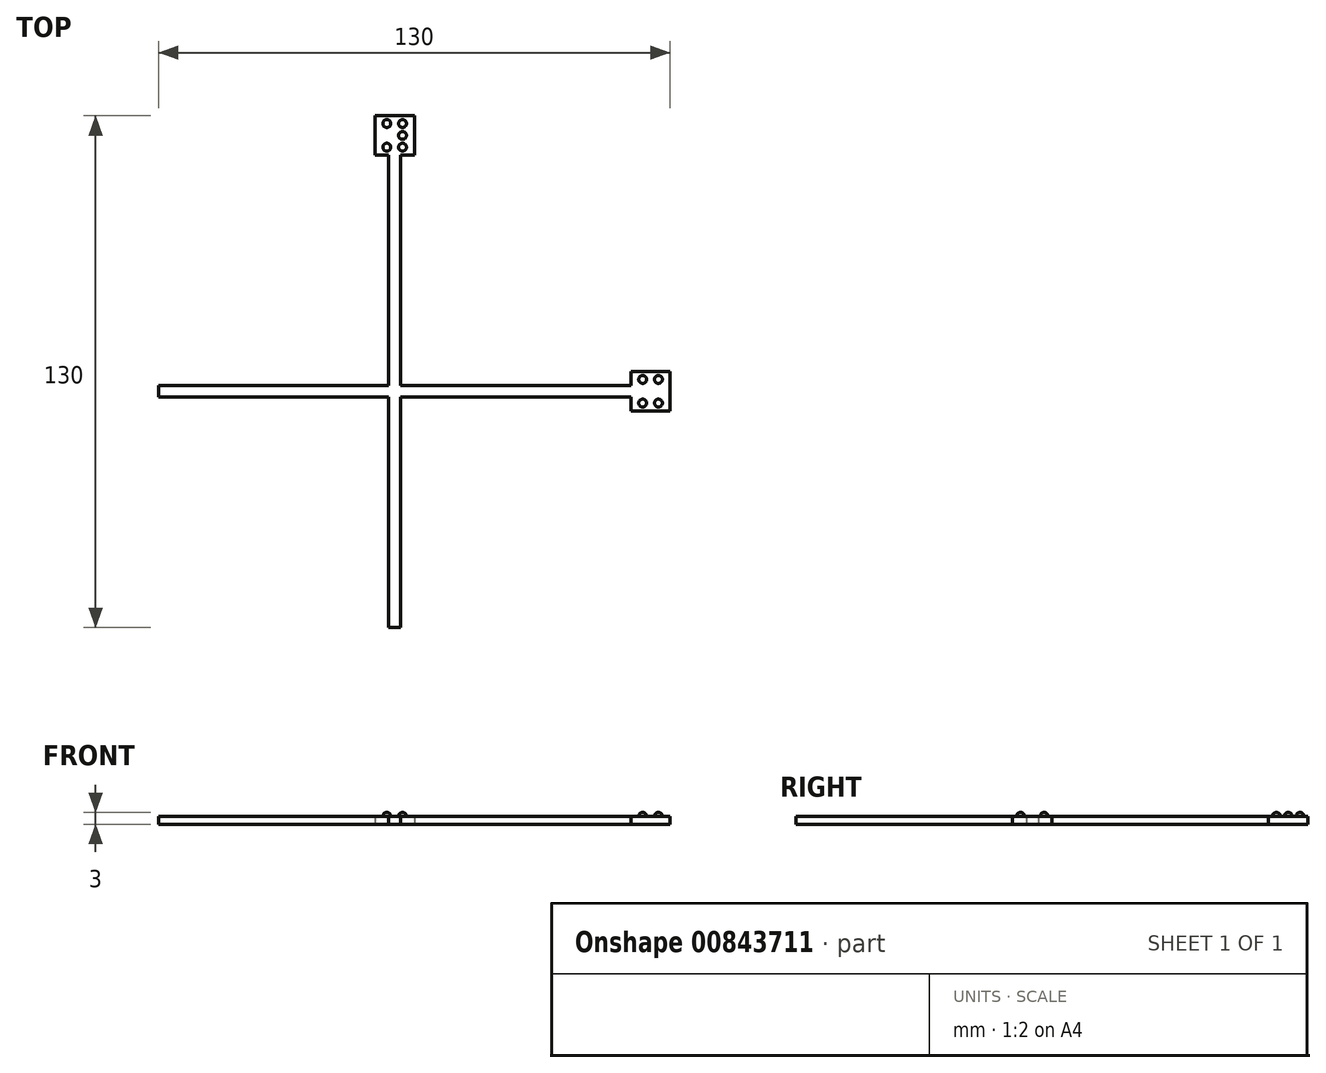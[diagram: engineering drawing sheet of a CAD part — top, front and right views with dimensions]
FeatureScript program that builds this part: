
annotation { "Feature Type Name" : "Feature", "Feature Type Description" : "" }
export const myFeature = defineFeature(function(context is Context, id is Id, definition is map)
    precondition{}
    {
        {
            var Q0;
            Q0=qCreatedBy(makeId("Top.planeOp"),FACE);
            var sketch = newSketch(context, id + "F0", { "sketchPlane" : qUnion([Q0])});
            skLineSegment(sketch, "E0.bottom", {"start": v(-60, 1.5) * mm, "end": v(60, 1.5) * mm});
            skLineSegment(sketch, "E0.top", {"start": v(-60, -1.5) * mm, "end": v(60, -1.5) * mm});
            skLineSegment(sketch, "E0.left", {"start": v(-60, 1.5) * mm, "end": v(-60, -1.5) * mm});
            skLineSegment(sketch, "E0.right", {"start": v(60, 1.5) * mm, "end": v(60, -1.5) * mm});
            skLineSegment(sketch, "E1.bottom", {"start": v(-1.5, 60) * mm, "end": v(1.5, 60) * mm});
            skLineSegment(sketch, "E1.top", {"start": v(-1.5, -60) * mm, "end": v(1.5, -60) * mm});
            skLineSegment(sketch, "E1.left", {"start": v(-1.5, 60) * mm, "end": v(-1.5, -60) * mm});
            skLineSegment(sketch, "E1.right", {"start": v(1.5, 60) * mm, "end": v(1.5, -60) * mm});
            skPoint(sketch, "E1.middle", {"position": v(0, 0) * mm});
            skLineSegment(sketch, "E2.bottom", {"start": v(5, 60) * mm, "end": v(-5, 60) * mm});
            skLineSegment(sketch, "E2.top", {"start": v(5, 70) * mm, "end": v(-5, 70) * mm});
            skLineSegment(sketch, "E2.left", {"start": v(5, 60) * mm, "end": v(5, 70) * mm});
            skLineSegment(sketch, "E2.right", {"start": v(-5, 60) * mm, "end": v(-5, 70) * mm});
            skPoint(sketch, "E2.middle", {"position": v(0, 65) * mm});
            skPoint(sketch, "E3", {"position": v(0, 60) * mm});
            skLineSegment(sketch, "E4.bottom", {"start": v(63.5, -5) * mm, "end": v(66.5, -5) * mm});
            skLineSegment(sketch, "E5.bottom", {"start": v(70, -5) * mm, "end": v(60, -5) * mm});
            skLineSegment(sketch, "E5.top", {"start": v(70, 5) * mm, "end": v(60, 5) * mm});
            skLineSegment(sketch, "E5.left", {"start": v(70, -5) * mm, "end": v(70, 5) * mm});
            skLineSegment(sketch, "E5.right", {"start": v(60, -5) * mm, "end": v(60, 5) * mm});
            skPoint(sketch, "E5.middle", {"position": v(65, 0) * mm});
            skPoint(sketch, "E6", {"position": v(65, -5) * mm});
            skPoint(sketch, "E7", {"position": v(60, 0) * mm});
            skPoint(sketch, "E8", {"position": v(0, 1.5) * mm});
            skCircle(sketch, "E9", {"center": v(-2, 68) * mm, "radius": 1 * mm});
            skCircle(sketch, "E10.1.0.0", {"center": v(2, 68) * mm, "radius": 1 * mm});
            skLineSegment(sketch, "E10.direction1", {"start": v(-2, 68) * mm, "end": v(2, 68) * mm, "construction": true});
            skCircle(sketch, "E11.1.0.0", {"center": v(-2, 62) * mm, "radius": 1 * mm});
            skLineSegment(sketch, "E11.direction1", {"start": v(-2, 68) * mm, "end": v(-2, 62) * mm, "construction": true});
            skCircle(sketch, "E12.1.0.0", {"center": v(2, 62) * mm, "radius": 1 * mm});
            skLineSegment(sketch, "E12.direction1", {"start": v(-2, 62) * mm, "end": v(2, 62) * mm, "construction": true});
            skCircle(sketch, "E13.1.0.0", {"center": v(2, 65) * mm, "radius": 1 * mm});
            skLineSegment(sketch, "E13.direction1", {"start": v(2, 68) * mm, "end": v(2, 65) * mm, "construction": true});
            skLineSegment(sketch, "E14", {"start": v(-2, 69) * mm, "end": v(-2, 61) * mm});
            skLineSegment(sketch, "E15", {"start": v(2, 69) * mm, "end": v(2, 61) * mm});
            skSolve(sketch);
        }
        {
            var Q0;
            Q0=makeQuery(id+"F0.imprint","IMPRINT",FACE,{"disambiguationData":[TD([[makeQuery(id+"F0.imprint","IMPRINT",EDGE,{"derivedFrom":sQuery(id+"F0.wireOp",EDGE,"E2.top")}),1.0]])]});
            var Q1;
            {var subQ0=sQuery(id+"F0.wireOp",EDGE,"E1.left");var subQ1=sQuery(id+"F0.wireOp",EDGE,"E0.bottom");var subQ2=makeQuery(id+"F0.imprint","INTERSECT",VERTEX,{"derivedFrom":[subQ1,subQ0]});Q1=makeQuery(id+"F0.imprint","IMPRINT",FACE,{"disambiguationData":[TD([[makeQuery(id+"F0.imprint","IMPRINT",EDGE,{"disambiguationData":[TD([[subQ2,-1.0]])],"derivedFrom":subQ1}),1.0]])]});}
            var Q2;
            {var subQ0=sQuery(id+"F0.wireOp",EDGE,"E5.right");var subQ1=sQuery(id+"F0.wireOp",EDGE,"E0.bottom");var subQ2=makeQuery(id+"F0.imprint","INTERSECT",VERTEX,{"derivedFrom":[subQ1,subQ0]});Q2=makeQuery(id+"F0.imprint","IMPRINT",FACE,{"disambiguationData":[TD([[makeQuery(id+"F0.imprint","IMPRINT",EDGE,{"disambiguationData":[TD([[subQ2,1.0]])],"derivedFrom":subQ1}),-1.0]])]});}
            var Q3;
            {var subQ0=sQuery(id+"F0.wireOp",EDGE,"E0.left");Q3=makeQuery(id+"F0.imprint","IMPRINT",FACE,{"disambiguationData":[TD([[makeQuery(id+"F0.imprint","IMPRINT",EDGE,{"derivedFrom":subQ0}),1.0]])]});}
            var Q4;
            {var subQ5=sQuery(id+"F0.wireOp",EDGE,"E5.top");Q4=makeQuery(id+"F0.imprint","IMPRINT",FACE,{"disambiguationData":[TD([[makeQuery(id+"F0.imprint","IMPRINT",EDGE,{"derivedFrom":subQ5}),1.0]])]});}
            var Q5;
            {var subQ5=sQuery(id+"F0.wireOp",EDGE,"E1.top");Q5=makeQuery(id+"F0.imprint","IMPRINT",FACE,{"disambiguationData":[TD([[makeQuery(id+"F0.imprint","IMPRINT",EDGE,{"derivedFrom":subQ5}),1.0]])]});}
            var Q6;
            {var subQ0=sQuery(id+"F0.wireOp",EDGE,"E1.left");var subQ1=sQuery(id+"F0.wireOp",EDGE,"E0.bottom");var subQ2=makeQuery(id+"F0.imprint","INTERSECT",VERTEX,{"derivedFrom":[subQ1,subQ0]});Q6=makeQuery(id+"F0.imprint","IMPRINT",FACE,{"disambiguationData":[TD([[makeQuery(id+"F0.imprint","IMPRINT",EDGE,{"disambiguationData":[TD([[subQ2,-1.0]])],"derivedFrom":subQ1}),-1.0]])]});}
            var Q7;
            {var subQ0=sQuery(id+"F0.wireOp",EDGE,"E14");var subQ1=sQuery(id+"F0.wireOp",EDGE,"E11.1.0.0");var subQ2=makeQuery(id+"F0.imprint","INTERSECT",VERTEX,{"disambiguationData":[OD(0.0)],"derivedFrom":[subQ1,subQ0]});Q7=makeQuery(id+"F0.imprint","IMPRINT",FACE,{"disambiguationData":[TD([[makeQuery(id+"F0.imprint","IMPRINT",EDGE,{"disambiguationData":[TD([[subQ2,1.0]])],"derivedFrom":subQ1}),1.0]])]});}
            var Q8;
            {var subQ0=sQuery(id+"F0.wireOp",EDGE,"E14");var subQ1=sQuery(id+"F0.wireOp",EDGE,"E11.1.0.0");var subQ2=makeQuery(id+"F0.imprint","INTERSECT",VERTEX,{"disambiguationData":[OD(0.0)],"derivedFrom":[subQ1,subQ0]});Q8=makeQuery(id+"F0.imprint","IMPRINT",FACE,{"disambiguationData":[TD([[makeQuery(id+"F0.imprint","IMPRINT",EDGE,{"disambiguationData":[TD([[subQ2,-1.0]])],"derivedFrom":subQ1}),1.0]])]});}
            var Q9;
            {var subQ0=sQuery(id+"F0.wireOp",EDGE,"E15");var subQ1=sQuery(id+"F0.wireOp",EDGE,"E12.1.0.0");var subQ2=makeQuery(id+"F0.imprint","INTERSECT",VERTEX,{"disambiguationData":[OD(0.0)],"derivedFrom":[subQ1,subQ0]});Q9=makeQuery(id+"F0.imprint","IMPRINT",FACE,{"disambiguationData":[TD([[makeQuery(id+"F0.imprint","IMPRINT",EDGE,{"disambiguationData":[TD([[subQ2,1.0]])],"derivedFrom":subQ1}),1.0]])]});}
            var Q10;
            {var subQ0=sQuery(id+"F0.wireOp",EDGE,"E15");var subQ1=sQuery(id+"F0.wireOp",EDGE,"E12.1.0.0");var subQ2=makeQuery(id+"F0.imprint","INTERSECT",VERTEX,{"disambiguationData":[OD(0.0)],"derivedFrom":[subQ1,subQ0]});Q10=makeQuery(id+"F0.imprint","IMPRINT",FACE,{"disambiguationData":[TD([[makeQuery(id+"F0.imprint","IMPRINT",EDGE,{"disambiguationData":[TD([[subQ2,-1.0]])],"derivedFrom":subQ1}),1.0]])]});}
            var Q11;
            {var subQ0=sQuery(id+"F0.wireOp",EDGE,"E14");var subQ1=sQuery(id+"F0.wireOp",EDGE,"E9");var subQ2=makeQuery(id+"F0.imprint","INTERSECT",VERTEX,{"disambiguationData":[OD(0.0)],"derivedFrom":[subQ1,subQ0]});Q11=makeQuery(id+"F0.imprint","IMPRINT",FACE,{"disambiguationData":[TD([[makeQuery(id+"F0.imprint","IMPRINT",EDGE,{"disambiguationData":[TD([[subQ2,-1.0]])],"derivedFrom":subQ1}),1.0]])]});}
            var Q12;
            {var subQ0=sQuery(id+"F0.wireOp",EDGE,"E14");var subQ1=sQuery(id+"F0.wireOp",EDGE,"E9");var subQ2=makeQuery(id+"F0.imprint","INTERSECT",VERTEX,{"disambiguationData":[OD(0.0)],"derivedFrom":[subQ1,subQ0]});Q12=makeQuery(id+"F0.imprint","IMPRINT",FACE,{"disambiguationData":[TD([[makeQuery(id+"F0.imprint","IMPRINT",EDGE,{"disambiguationData":[TD([[subQ2,1.0]])],"derivedFrom":subQ1}),1.0]])]});}
            var Q13;
            {var subQ0=sQuery(id+"F0.wireOp",EDGE,"E15");var subQ1=sQuery(id+"F0.wireOp",EDGE,"E13.1.0.0");var subQ2=makeQuery(id+"F0.imprint","INTERSECT",VERTEX,{"disambiguationData":[OD(0.0)],"derivedFrom":[subQ1,subQ0]});Q13=makeQuery(id+"F0.imprint","IMPRINT",FACE,{"disambiguationData":[TD([[makeQuery(id+"F0.imprint","IMPRINT",EDGE,{"disambiguationData":[TD([[subQ2,1.0]])],"derivedFrom":subQ1}),1.0]])]});}
            var Q14;
            {var subQ0=sQuery(id+"F0.wireOp",EDGE,"E15");var subQ1=sQuery(id+"F0.wireOp",EDGE,"E13.1.0.0");var subQ2=makeQuery(id+"F0.imprint","INTERSECT",VERTEX,{"disambiguationData":[OD(0.0)],"derivedFrom":[subQ1,subQ0]});Q14=makeQuery(id+"F0.imprint","IMPRINT",FACE,{"disambiguationData":[TD([[makeQuery(id+"F0.imprint","IMPRINT",EDGE,{"disambiguationData":[TD([[subQ2,-1.0]])],"derivedFrom":subQ1}),1.0]])]});}
            var Q15;
            {var subQ0=sQuery(id+"F0.wireOp",EDGE,"E15");var subQ1=sQuery(id+"F0.wireOp",EDGE,"E10.1.0.0");var subQ2=makeQuery(id+"F0.imprint","INTERSECT",VERTEX,{"disambiguationData":[OD(0.0)],"derivedFrom":[subQ1,subQ0]});Q15=makeQuery(id+"F0.imprint","IMPRINT",FACE,{"disambiguationData":[TD([[makeQuery(id+"F0.imprint","IMPRINT",EDGE,{"disambiguationData":[TD([[subQ2,-1.0]])],"derivedFrom":subQ1}),1.0]])]});}
            var Q16;
            {var subQ0=sQuery(id+"F0.wireOp",EDGE,"E15");var subQ1=sQuery(id+"F0.wireOp",EDGE,"E10.1.0.0");var subQ2=makeQuery(id+"F0.imprint","INTERSECT",VERTEX,{"disambiguationData":[OD(0.0)],"derivedFrom":[subQ1,subQ0]});Q16=makeQuery(id+"F0.imprint","IMPRINT",FACE,{"disambiguationData":[TD([[makeQuery(id+"F0.imprint","IMPRINT",EDGE,{"disambiguationData":[TD([[subQ2,1.0]])],"derivedFrom":subQ1}),1.0]])]});}
            extrude(context, id + "F1", {"entities" : qUnion([Q0, Q1, Q2, Q3, Q4, Q5, Q6, Q7, Q8, Q9, Q10, Q11, Q12, Q13, Q14, Q15, Q16]), "endBound" : BoundingType.SYMMETRIC, "depth" : 2 * mm, "offsetDistance" : 25 * mm});
        }
        {
            var Q0;
            Q0=makeQuery(id+"F1.opExtrude","CAP_FACE",FACE,{"disambiguationData":[OSD([sQuery(id+"F0.wireOp",EDGE,"E0.bottom"),sQuery(id+"F0.wireOp",EDGE,"E0.top"),sQuery(id+"F0.wireOp",EDGE,"E0.left"),sQuery(id+"F0.wireOp",EDGE,"E1.top"),sQuery(id+"F0.wireOp",EDGE,"E1.left"),sQuery(id+"F0.wireOp",EDGE,"E1.right"),sQuery(id+"F0.wireOp",EDGE,"E2.bottom"),sQuery(id+"F0.wireOp",EDGE,"E2.top"),sQuery(id+"F0.wireOp",EDGE,"E2.left"),sQuery(id+"F0.wireOp",EDGE,"E2.right"),sQuery(id+"F0.wireOp",EDGE,"E5.bottom"),sQuery(id+"F0.wireOp",EDGE,"E5.top"),sQuery(id+"F0.wireOp",EDGE,"E5.left"),sQuery(id+"F0.wireOp",EDGE,"E5.right")])],"isStart":false});
            var sketch = newSketch(context, id + "F2", { "sketchPlane" : qUnion([Q0])});
            skPoint(sketch, "E16.middle", {"position": v(0, 65.1) * mm});
            skCircle(sketch, "E17", {"center": v(-2, 68) * mm, "radius": 1 * mm});
            skCircle(sketch, "E18.1.0.0", {"center": v(2, 68) * mm, "radius": 1 * mm});
            skLineSegment(sketch, "E18.direction1", {"start": v(-2, 68) * mm, "end": v(2, 68) * mm, "construction": true});
            skCircle(sketch, "E19.1.0.0", {"center": v(-2, 62) * mm, "radius": 1 * mm});
            skLineSegment(sketch, "E19.direction1", {"start": v(-2, 68) * mm, "end": v(-2, 62) * mm, "construction": true});
            skCircle(sketch, "E20.1.0.0", {"center": v(2, 62) * mm, "radius": 1 * mm});
            skLineSegment(sketch, "E20.direction1", {"start": v(-2, 62) * mm, "end": v(2, 62) * mm, "construction": true});
            skCircle(sketch, "E21.1.0.0", {"center": v(2, 65) * mm, "radius": 1 * mm});
            skLineSegment(sketch, "E21.direction1", {"start": v(2, 68) * mm, "end": v(2, 65) * mm, "construction": true});
            skLineSegment(sketch, "E22", {"start": v(-2, 69) * mm, "end": v(-2, 61) * mm});
            skLineSegment(sketch, "E23", {"start": v(2, 69) * mm, "end": v(2, 61) * mm});
            skCircle(sketch, "E24.1.0.0", {"center": v(-2, 65) * mm, "radius": 1 * mm});
            skLineSegment(sketch, "E24.direction1", {"start": v(2, 65) * mm, "end": v(-2, 65) * mm, "construction": true});
            skPoint(sketch, "E25.middle", {"position": v(65.04, 0) * mm});
            skCircle(sketch, "E26", {"center": v(63, 3) * mm, "radius": 1 * mm});
            skCircle(sketch, "E27.1.0.0", {"center": v(67, 3) * mm, "radius": 1 * mm});
            skLineSegment(sketch, "E27.direction1", {"start": v(63, 3) * mm, "end": v(67, 3) * mm, "construction": true});
            skCircle(sketch, "E28.1.0.0", {"center": v(63, -3) * mm, "radius": 1 * mm});
            skLineSegment(sketch, "E28.direction1", {"start": v(63, 3) * mm, "end": v(63, -3) * mm, "construction": true});
            skCircle(sketch, "E29.1.0.0", {"center": v(67, -3) * mm, "radius": 1 * mm});
            skLineSegment(sketch, "E29.direction1", {"start": v(63, -3) * mm, "end": v(67, -3) * mm, "construction": true});
            skCircle(sketch, "E30.1.0.0", {"center": v(67, 0) * mm, "radius": 1 * mm});
            skLineSegment(sketch, "E30.direction1", {"start": v(67, 3) * mm, "end": v(67, 0) * mm, "construction": true});
            skLineSegment(sketch, "E31", {"start": v(63, 4) * mm, "end": v(63, -4) * mm});
            skLineSegment(sketch, "E32", {"start": v(67, 4) * mm, "end": v(67, -4) * mm});
            skCircle(sketch, "E33.1.0.0", {"center": v(63, 0) * mm, "radius": 1 * mm});
            skLineSegment(sketch, "E33.direction1", {"start": v(67, 0) * mm, "end": v(63, 0) * mm, "construction": true});
            skPoint(sketch, "E34", {"position": v(60, 0) * mm});
            skSolve(sketch);
        }
        {
            var Q0;
            {var subQ0=sQuery(id+"F2.wireOp",EDGE,"E22");var subQ1=sQuery(id+"F2.wireOp",EDGE,"E17");var subQ2=makeQuery(id+"F2.imprint","INTERSECT",VERTEX,{"disambiguationData":[OD(0.0)],"derivedFrom":[subQ1,subQ0]});Q0=makeQuery(id+"F2.imprint","IMPRINT",FACE,{"disambiguationData":[TD([[makeQuery(id+"F2.imprint","IMPRINT",EDGE,{"disambiguationData":[TD([[subQ2,-1.0]])],"derivedFrom":subQ1}),1.0]])]});}
            var Q1;
            {var subQ0=sQuery(id+"F2.wireOp",EDGE,"E22");var subQ1=sQuery(id+"F2.wireOp",EDGE,"E19.1.0.0");var subQ2=makeQuery(id+"F2.imprint","INTERSECT",VERTEX,{"disambiguationData":[OD(0.0)],"derivedFrom":[subQ1,subQ0]});Q1=makeQuery(id+"F2.imprint","IMPRINT",FACE,{"disambiguationData":[TD([[makeQuery(id+"F2.imprint","IMPRINT",EDGE,{"disambiguationData":[TD([[subQ2,1.0]])],"derivedFrom":subQ1}),1.0]])]});}
            var Q2;
            Q2=sQuery(id+"F2.wireOp",EDGE,"E22");
            revolve(context, id + "F3", {"operationType" : NewBodyOperationType.ADD, "surfaceOperationType" : NewSurfaceOperationType.NEW, "entities" : qUnion([Q0, Q1]), "axis" : qUnion([Q2]), "revolveType" : RevolveType.FULL});
        }
        {
            var Q0;
            {var subQ0=sQuery(id+"F2.wireOp",EDGE,"E23");var subQ1=sQuery(id+"F2.wireOp",EDGE,"E18.1.0.0");var subQ2=makeQuery(id+"F2.imprint","INTERSECT",VERTEX,{"disambiguationData":[OD(0.0)],"derivedFrom":[subQ1,subQ0]});Q0=makeQuery(id+"F2.imprint","IMPRINT",FACE,{"disambiguationData":[TD([[makeQuery(id+"F2.imprint","IMPRINT",EDGE,{"disambiguationData":[TD([[subQ2,1.0]])],"derivedFrom":subQ1}),1.0]])]});}
            var Q1;
            {var subQ0=sQuery(id+"F2.wireOp",EDGE,"E23");var subQ1=sQuery(id+"F2.wireOp",EDGE,"E21.1.0.0");var subQ2=makeQuery(id+"F2.imprint","INTERSECT",VERTEX,{"disambiguationData":[OD(0.0)],"derivedFrom":[subQ1,subQ0]});Q1=makeQuery(id+"F2.imprint","IMPRINT",FACE,{"disambiguationData":[TD([[makeQuery(id+"F2.imprint","IMPRINT",EDGE,{"disambiguationData":[TD([[subQ2,-1.0]])],"derivedFrom":subQ1}),1.0]])]});}
            var Q2;
            {var subQ0=sQuery(id+"F2.wireOp",EDGE,"E23");var subQ1=sQuery(id+"F2.wireOp",EDGE,"E20.1.0.0");var subQ2=makeQuery(id+"F2.imprint","INTERSECT",VERTEX,{"disambiguationData":[OD(0.0)],"derivedFrom":[subQ1,subQ0]});Q2=makeQuery(id+"F2.imprint","IMPRINT",FACE,{"disambiguationData":[TD([[makeQuery(id+"F2.imprint","IMPRINT",EDGE,{"disambiguationData":[TD([[subQ2,-1.0]])],"derivedFrom":subQ1}),1.0]])]});}
            var Q3;
            Q3=sQuery(id+"F2.wireOp",EDGE,"E23");
            revolve(context, id + "F4", {"operationType" : NewBodyOperationType.ADD, "surfaceOperationType" : NewSurfaceOperationType.NEW, "entities" : qUnion([Q0, Q1, Q2]), "axis" : qUnion([Q3]), "revolveType" : RevolveType.FULL});
        }
        {
            var Q0;
            {var subQ0=sQuery(id+"F2.wireOp",EDGE,"E31");var subQ1=sQuery(id+"F2.wireOp",EDGE,"E26");var subQ2=makeQuery(id+"F2.imprint","INTERSECT",VERTEX,{"disambiguationData":[OD(0.0)],"derivedFrom":[subQ1,subQ0]});Q0=makeQuery(id+"F2.imprint","IMPRINT",FACE,{"disambiguationData":[TD([[makeQuery(id+"F2.imprint","IMPRINT",EDGE,{"disambiguationData":[TD([[subQ2,-1.0]])],"derivedFrom":subQ1}),1.0]])]});}
            var Q1;
            {var subQ0=sQuery(id+"F2.wireOp",EDGE,"E31");var subQ1=sQuery(id+"F2.wireOp",EDGE,"E28.1.0.0");var subQ2=makeQuery(id+"F2.imprint","INTERSECT",VERTEX,{"disambiguationData":[OD(0.0)],"derivedFrom":[subQ1,subQ0]});Q1=makeQuery(id+"F2.imprint","IMPRINT",FACE,{"disambiguationData":[TD([[makeQuery(id+"F2.imprint","IMPRINT",EDGE,{"disambiguationData":[TD([[subQ2,1.0]])],"derivedFrom":subQ1}),1.0]])]});}
            var Q2;
            Q2=sQuery(id+"F2.wireOp",EDGE,"E31");
            revolve(context, id + "F5", {"operationType" : NewBodyOperationType.ADD, "surfaceOperationType" : NewSurfaceOperationType.NEW, "entities" : qUnion([Q0, Q1]), "axis" : qUnion([Q2]), "revolveType" : RevolveType.FULL});
        }
        {
            var Q0;
            {var subQ0=sQuery(id+"F2.wireOp",EDGE,"E32");var subQ1=sQuery(id+"F2.wireOp",EDGE,"E27.1.0.0");var subQ2=makeQuery(id+"F2.imprint","INTERSECT",VERTEX,{"disambiguationData":[OD(0.0)],"derivedFrom":[subQ1,subQ0]});Q0=makeQuery(id+"F2.imprint","IMPRINT",FACE,{"disambiguationData":[TD([[makeQuery(id+"F2.imprint","IMPRINT",EDGE,{"disambiguationData":[TD([[subQ2,1.0]])],"derivedFrom":subQ1}),1.0]])]});}
            var Q1;
            {var subQ0=sQuery(id+"F2.wireOp",EDGE,"E32");var subQ1=sQuery(id+"F2.wireOp",EDGE,"E29.1.0.0");var subQ2=makeQuery(id+"F2.imprint","INTERSECT",VERTEX,{"disambiguationData":[OD(0.0)],"derivedFrom":[subQ1,subQ0]});Q1=makeQuery(id+"F2.imprint","IMPRINT",FACE,{"disambiguationData":[TD([[makeQuery(id+"F2.imprint","IMPRINT",EDGE,{"disambiguationData":[TD([[subQ2,-1.0]])],"derivedFrom":subQ1}),1.0]])]});}
            var Q2;
            Q2=sQuery(id+"F2.wireOp",EDGE,"E32");
            revolve(context, id + "F6", {"operationType" : NewBodyOperationType.ADD, "surfaceOperationType" : NewSurfaceOperationType.NEW, "entities" : qUnion([Q0, Q1]), "axis" : qUnion([Q2]), "revolveType" : RevolveType.FULL});
        }
    });
